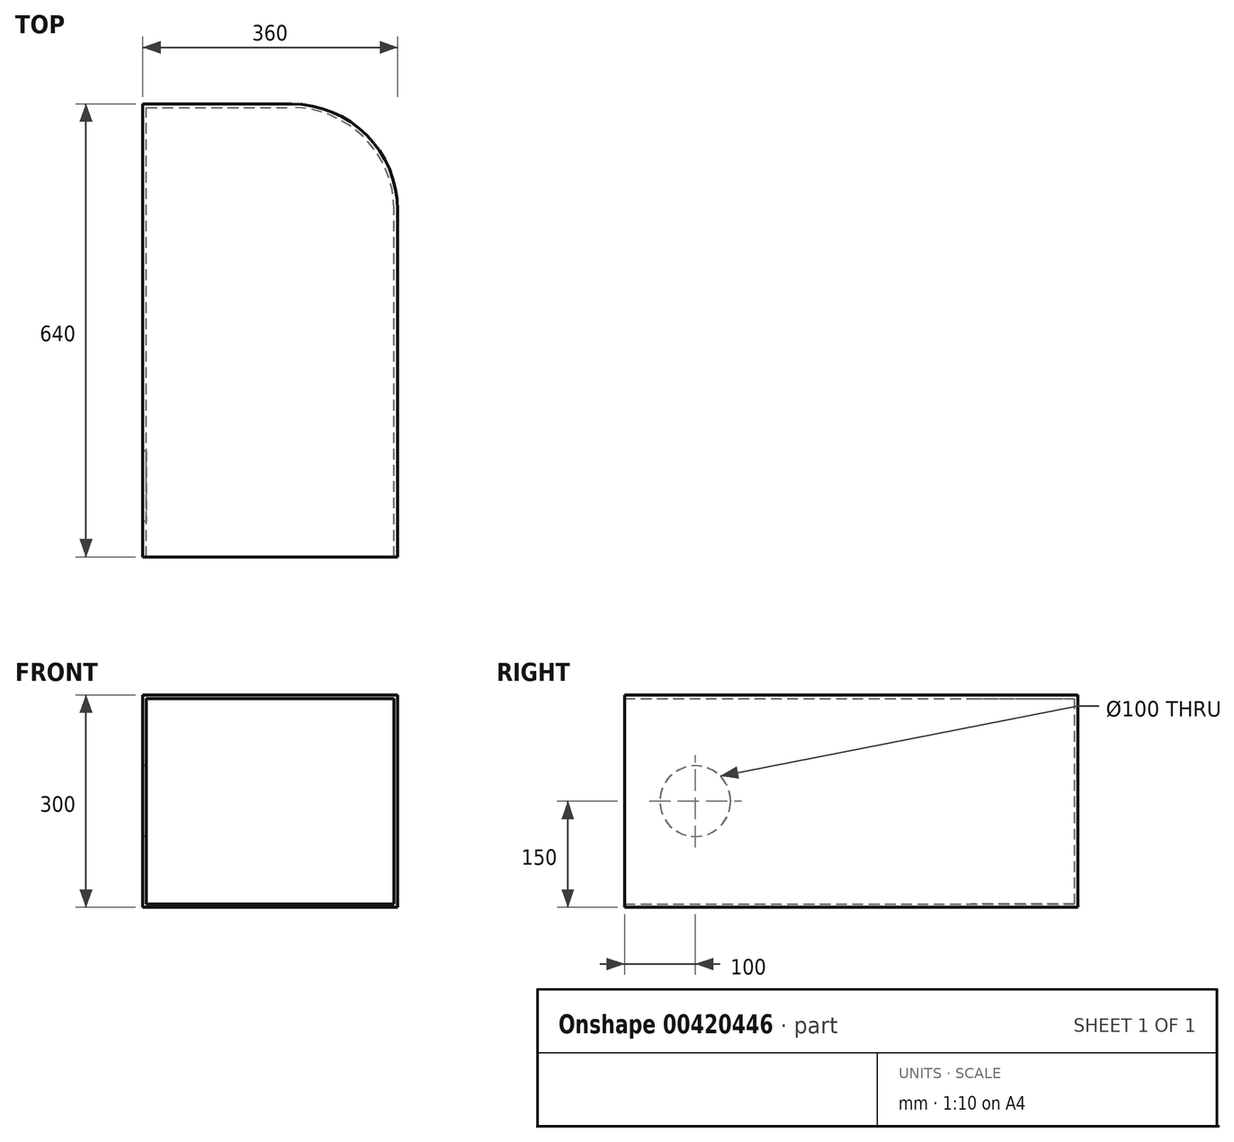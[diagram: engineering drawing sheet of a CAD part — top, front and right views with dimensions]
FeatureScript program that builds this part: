
annotation { "Feature Type Name" : "Feature", "Feature Type Description" : "" }
export const myFeature = defineFeature(function(context is Context, id is Id, definition is map)
    precondition{}
    {
        {
            var Q0;
            Q0=qCreatedBy(makeId("Top.planeOp"),FACE);
            var sketch = newSketch(context, id + "F0", { "sketchPlane" : qUnion([Q0])});
            skLineSegment(sketch, "E0.bottom", {"start": v(0, 0) * mm, "end": v(360, 0) * mm});
            skLineSegment(sketch, "E0.top", {"start": v(0, 640) * mm, "end": v(210, 640) * mm});
            skLineSegment(sketch, "E0.left", {"start": v(0, 0) * mm, "end": v(0, 640) * mm});
            skLineSegment(sketch, "E0.right", {"start": v(360, 0) * mm, "end": v(360, 490) * mm});
            skPoint(sketch, "E1.visualSharp", {"position": v(360, 640) * mm});
            skArc(sketch, "E1.filletArc", {"start": v(360, 490) * mm, "mid": v(316.07, 596.07) * mm, "end": v(210, 640) * mm});
            skSolve(sketch);
        }
        {
            var Q0;
            Q0=makeQuery(id+"F0.imprint","IMPRINT",FACE,{"disambiguationData":[TD([[makeQuery(id+"F0.imprint","IMPRINT",EDGE,{"derivedFrom":sQuery(id+"F0.wireOp",EDGE,"E0.bottom")}),1.0]])]});
            extrude(context, id + "F1", {"entities" : qUnion([Q0]), "depth" : 150 * mm});
        }
        {
            var Q0;
            Q0=makeQuery(id+"F1.opExtrude","SWEPT_BODY",BODY,{"disambiguationData":[OSD([sQuery(id+"F0.wireOp",EDGE,"E0.bottom"),sQuery(id+"F0.wireOp",EDGE,"E0.top"),sQuery(id+"F0.wireOp",EDGE,"E0.left"),sQuery(id+"F0.wireOp",EDGE,"E0.right"),sQuery(id+"F0.wireOp",EDGE,"E1.filletArc")])]});
            var Q1;
            Q1=qCreatedBy(makeId("Top.planeOp"),FACE);
            mirror(context, id + "F2", {"operationType" : NewBodyOperationType.ADD, "entities" : qUnion([Q0]), "mirrorPlane" : qUnion([Q1])});
        }
        {
            var Q0;
            {var subQ0=makeQuery(id+"F1.opExtrude","SWEPT_FACE",FACE,{"disambiguationData":[OSD([sQuery(id+"F0.wireOp",EDGE,"E0.bottom")])]});Q0=makeQuery(id+"F2.boolean.opBoolean","MERGE",FACE,{"derivedFrom":[subQ0,makeQuery(id+"F2.opPattern","COPY",FACE,{"derivedFrom":subQ0,"instanceName":"1"})]});}
            shell(context, id + "F3", {"entities" : qUnion([Q0]), "thickness" : 5 * mm});
        }
        {
            var Q0;
            {var subQ0=makeQuery(id+"F1.opExtrude","SWEPT_FACE",FACE,{"disambiguationData":[OSD([sQuery(id+"F0.wireOp",EDGE,"E0.left")])]});Q0=makeQuery(id+"F2.boolean.opBoolean","MERGE",FACE,{"derivedFrom":[subQ0,makeQuery(id+"F2.opPattern","COPY",FACE,{"derivedFrom":subQ0,"instanceName":"1"})]});}
            var sketch = newSketch(context, id + "F4", { "sketchPlane" : qUnion([Q0])});
            skCircle(sketch, "E2", {"center": v(-100, 0) * mm, "radius": 50 * mm});
            skSolve(sketch);
        }
        {
            var Q0;
            Q0=makeQuery(id+"F4.imprint","IMPRINT",FACE,{"disambiguationData":[TD([[makeQuery(id+"F4.imprint","IMPRINT",EDGE,{"derivedFrom":sQuery(id+"F4.wireOp",EDGE,"E2")}),1.0]])]});
            var Q1;
            Q1=sQuery(id+"F4.wireOp",EDGE,"E2");
            extrude(context, id + "F5", {"entities" : qUnion([Q0]), "operationType" : NewBodyOperationType.REMOVE, "surfaceEntities" : qUnion([Q1]), "endBound" : BoundingType.UP_TO_NEXT, "oppositeDirection" : true, "depth" : 25 * mm});
        }
    });
